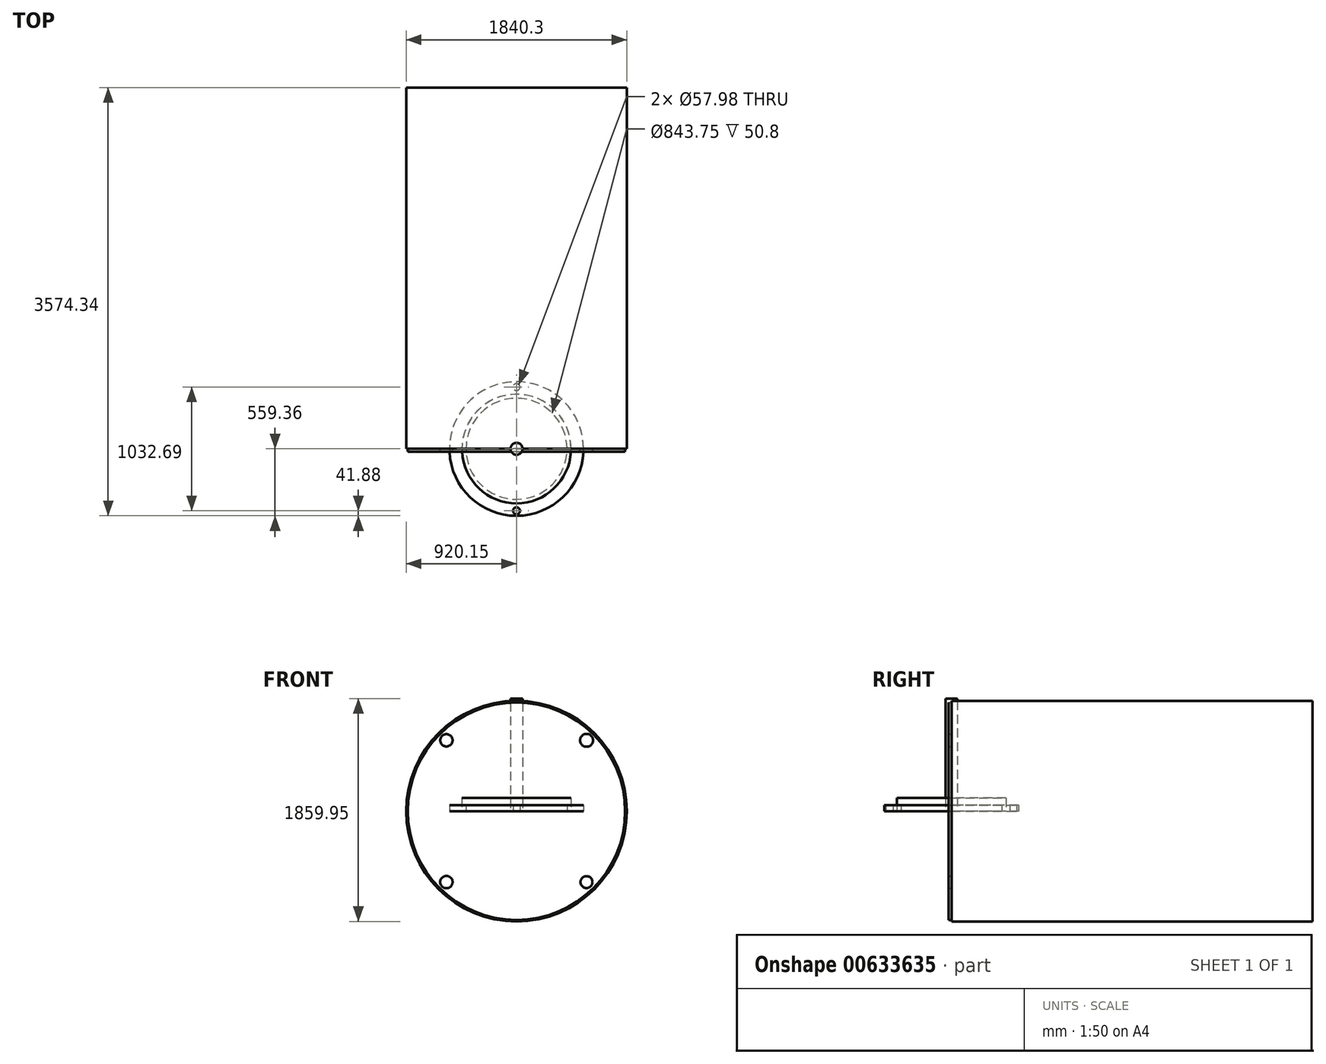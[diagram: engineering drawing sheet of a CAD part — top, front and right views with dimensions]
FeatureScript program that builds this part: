
annotation { "Feature Type Name" : "Feature", "Feature Type Description" : "" }
export const myFeature = defineFeature(function(context is Context, id is Id, definition is map)
    precondition{}
    {
        {
            var Q0;
            Q0=qCreatedBy(makeId("Front.planeOp"),FACE);
            var sketch = newSketch(context, id + "F0", { "sketchPlane" : qUnion([Q0])});
            skCircle(sketch, "E0", {"center": v(0, 0) * mm, "radius": 920.15 * mm});
            skSolve(sketch);
        }
        {
            var Q0;
            Q0=makeQuery(id+"F0.imprint","IMPRINT",FACE,{"disambiguationData":[TD([[makeQuery(id+"F0.imprint","IMPRINT",EDGE,{"derivedFrom":sQuery(id+"F0.wireOp",EDGE,"E0")}),1.0]])]});
            extrude(context, id + "F1", {"entities" : qUnion([Q0]), "oppositeDirection" : true, "depth" : 3014.98 * mm, "offsetDistance" : 25.4 * mm});
        }
        {
            var Q0;
            Q0=qCreatedBy(makeId("Top.planeOp"),FACE);
            var sketch = newSketch(context, id + "F2", { "sketchPlane" : qUnion([Q0])});
            skCircle(sketch, "E1", {"center": v(0, 0) * mm, "radius": 559.36 * mm});
            skCircle(sketch, "E2", {"center": v(0, 0) * mm, "radius": 421.87 * mm});
            skCircle(sketch, "E3", {"center": v(0, 515.2) * mm, "radius": 28.99 * mm});
            skCircle(sketch, "E4", {"center": v(0, -517.48) * mm, "radius": 28.99 * mm});
            skSolve(sketch);
        }
        {
            var Q0;
            Q0=makeQuery(id+"F2.imprint","IMPRINT",FACE,{"disambiguationData":[TD([[makeQuery(id+"F2.imprint","IMPRINT",EDGE,{"derivedFrom":sQuery(id+"F2.wireOp",EDGE,"E1")}),1.0]])]});
            extrude(context, id + "F3", {"entities" : qUnion([Q0]), "depth" : 50.8 * mm, "offsetDistance" : 25.4 * mm});
        }
        {
            var Q0;
            Q0=qCreatedBy(makeId("Top.planeOp"),FACE);
            var sketch = newSketch(context, id + "F4", { "sketchPlane" : qUnion([Q0])});
            skCircle(sketch, "E5", {"center": v(0, 0) * mm, "radius": 455.01 * mm});
            skSolve(sketch);
        }
        {
            var Q0;
            Q0=sQuery(id+"F4.wireOp",EDGE,"E5");
            var Q1;
            Q1=sQuery(id+"F4.wireOp",EDGE,"9ZSlDE8O-Hgyl-h0zI-duLY-3wCOhdRcVxG3");
            extrude(context, id + "F5", {"bodyType" : ToolBodyType.SURFACE, "surfaceEntities" : qUnion([Q0, Q1]), "depth" : 50.8 * mm, "offsetDistance" : 25.4 * mm});
        }
        {
            var Q0;
            Q0=makeQuery(id+"F4.imprint","IMPRINT",FACE,{"disambiguationData":[TD([[makeQuery(id+"F4.imprint","IMPRINT",EDGE,{"derivedFrom":sQuery(id+"F4.wireOp",EDGE,"E5")}),1.0]])]});
            extrude(context, id + "F6", {"entities" : qUnion([Q0]), "depth" : 109.22 * mm, "offsetDistance" : 25.4 * mm});
        }
        {
            var Q0;
            Q0=qCreatedBy(makeId("Front.planeOp"),FACE);
            var sketch = newSketch(context, id + "F7", { "sketchPlane" : qUnion([Q0])});
            skCircle(sketch, "E6", {"center": v(0, 0) * mm, "radius": 907.18 * mm});
            skCircle(sketch, "E7", {"center": v(-585, 591.48) * mm, "radius": 51.28 * mm});
            skCircle(sketch, "E8", {"center": v(585.15, 591.33) * mm, "radius": 53.67 * mm});
            skCircle(sketch, "E9", {"center": v(584.43, -592.04) * mm, "radius": 50.03 * mm});
            skCircle(sketch, "E10", {"center": v(-584.97, -591.5) * mm, "radius": 51.83 * mm});
            skSolve(sketch);
        }
        {
            var Q0;
            Q0 = qSketchRegion(id + "F7", true);
            extrude(context, id + "F8", {"entities" : qUnion([Q0]), "depth" : 25.4 * mm, "offsetDistance" : 25.4 * mm});
        }
        {
            var Q0;
            Q0=qCreatedBy(makeId("Top.planeOp"),FACE);
            var sketch = newSketch(context, id + "F9", { "sketchPlane" : qUnion([Q0])});
            skCircle(sketch, "E11", {"center": v(0, 0) * mm, "radius": 50.06 * mm});
            skSolve(sketch);
        }
        {
            var Q0;
            Q0=makeQuery(id+"F9.imprint","IMPRINT",FACE,{"disambiguationData":[TD([[makeQuery(id+"F9.imprint","IMPRINT",EDGE,{"derivedFrom":sQuery(id+"F9.wireOp",EDGE,"E11")}),1.0]])]});
            extrude(context, id + "F10", {"entities" : qUnion([Q0]), "depth" : 939.8 * mm, "offsetDistance" : 25.4 * mm});
        }
    });
